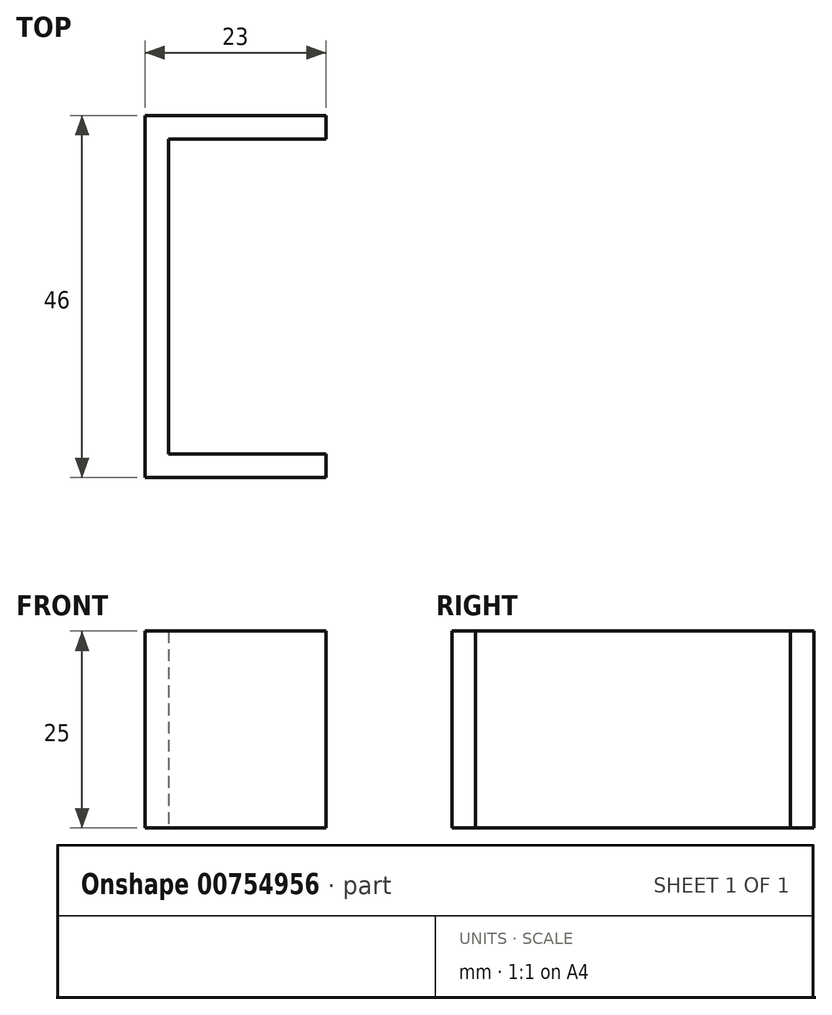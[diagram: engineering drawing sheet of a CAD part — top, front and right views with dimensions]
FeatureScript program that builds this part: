
annotation { "Feature Type Name" : "Feature", "Feature Type Description" : "" }
export const myFeature = defineFeature(function(context is Context, id is Id, definition is map)
    precondition{}
    {
        {
            var Q0;
            Q0=qCreatedBy(makeId("Top.planeOp"),FACE);
            var sketch = newSketch(context, id + "F0", { "sketchPlane" : qUnion([Q0])});
            skLineSegment(sketch, "E0", {"start": v(9.9, 30.79) * mm, "end": v(-13.1, 30.79) * mm});
            skLineSegment(sketch, "E1", {"start": v(-13.1, 30.79) * mm, "end": v(-13.1, -15.21) * mm});
            skLineSegment(sketch, "E2", {"start": v(-13.1, -15.21) * mm, "end": v(9.9, -15.21) * mm});
            skLineSegment(sketch, "E3", {"start": v(9.9, -15.21) * mm, "end": v(9.9, -12.21) * mm});
            skLineSegment(sketch, "E4", {"start": v(9.9, -12.21) * mm, "end": v(-10.1, -12.21) * mm});
            skLineSegment(sketch, "E5", {"start": v(-10.1, -12.21) * mm, "end": v(-10.1, 27.79) * mm});
            skLineSegment(sketch, "E6", {"start": v(-10.1, 27.79) * mm, "end": v(9.9, 27.79) * mm});
            skLineSegment(sketch, "E7", {"start": v(9.9, 27.79) * mm, "end": v(9.9, 30.79) * mm});
            skSolve(sketch);
        }
        {
            var Q0;
            Q0 = qSketchRegion(id + "F0", true);
            extrude(context, id + "F1", {"entities" : qUnion([Q0]), "depth" : 25 * mm, "offsetDistance" : 25 * mm});
        }
    });
